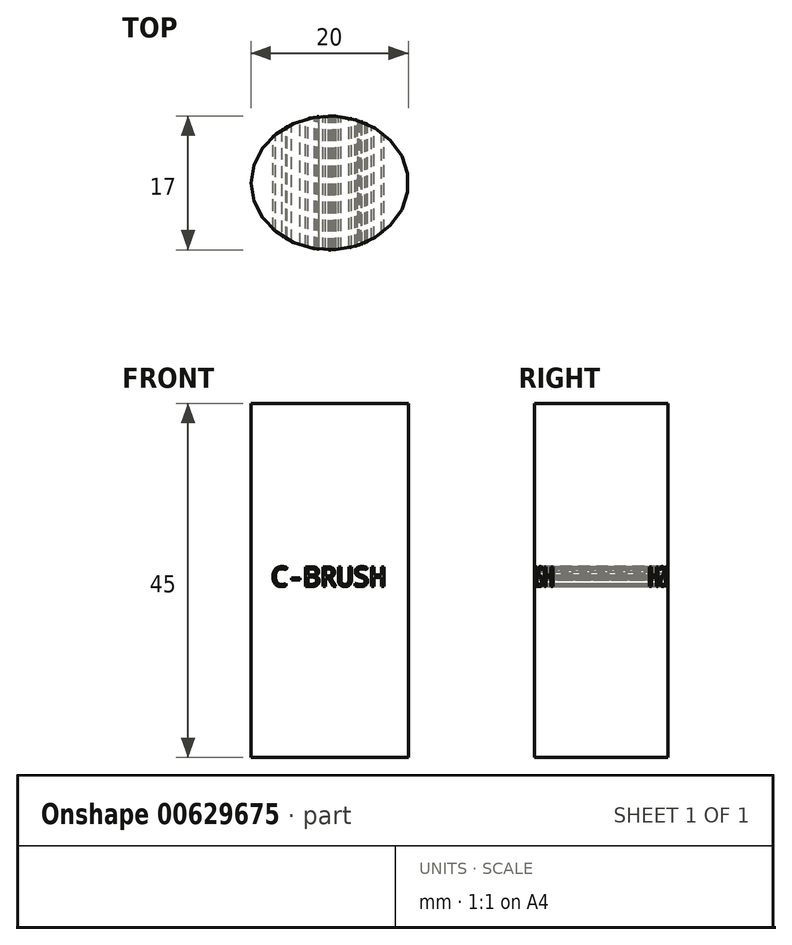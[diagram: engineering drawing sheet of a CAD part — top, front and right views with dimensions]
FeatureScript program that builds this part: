
annotation { "Feature Type Name" : "Feature", "Feature Type Description" : "" }
export const myFeature = defineFeature(function(context is Context, id is Id, definition is map)
    precondition{}
    {
        {
            var Q0;
            Q0=qCreatedBy(makeId("Top.planeOp"),FACE);
            var sketch = newSketch(context, id + "F0", { "sketchPlane" : qUnion([Q0])});
            skEllipse(sketch, "E0", {"center": v(0, 0) * mm, "majorRadius": 10 * mm, "minorRadius": 8.5 * mm, "majorAxis": v(-1, 0)});
            skFitSpline(sketch, "E1.0", {"points": [v(-11.96, 1.07) * mm, v(-12.02, 0) * mm, v(-11.96, -1.07) * mm, v(-11.71, -2.47) * mm, v(-11.23, -3.82) * mm, v(-10.53, -5.08) * mm, v(-9.7, -6.27) * mm, v(-8.42, -7.58) * mm, v(-6.9, -8.65) * mm, v(-5.55, -9.33) * mm, v(-4.14, -9.9) * mm, v(-2.67, -10.28) * mm, v(-1.15, -10.47) * mm, v(0, -10.52) * mm, v(1.15, -10.47) * mm, v(2.67, -10.28) * mm, v(4.14, -9.9) * mm, v(5.55, -9.33) * mm, v(6.9, -8.65) * mm, v(8.42, -7.58) * mm, v(9.7, -6.27) * mm, v(10.53, -5.08) * mm, v(11.23, -3.82) * mm, v(11.71, -2.47) * mm, v(11.96, -1.07) * mm, v(12.02, 0) * mm, v(11.96, 1.07) * mm, v(11.71, 2.47) * mm, v(11.23, 3.82) * mm, v(10.53, 5.08) * mm, v(9.7, 6.27) * mm, v(8.42, 7.58) * mm, v(6.9, 8.65) * mm, v(5.55, 9.33) * mm, v(4.14, 9.9) * mm, v(2.67, 10.28) * mm, v(1.15, 10.47) * mm, v(0, 10.52) * mm, v(-1.15, 10.47) * mm, v(-2.67, 10.28) * mm, v(-4.14, 9.9) * mm, v(-5.55, 9.33) * mm, v(-6.9, 8.65) * mm, v(-8.42, 7.58) * mm, v(-9.7, 6.27) * mm, v(-10.53, 5.08) * mm, v(-11.23, 3.82) * mm, v(-11.71, 2.47) * mm, v(-11.96, 1.07) * mm, v(-12.02, 0) * mm, v(-11.96, -1.07) * mm, v(-11.96, 1.07) * mm]});
            skSolve(sketch);
        }
        {
            var Q0;
            Q0=qSketchRegion(id+"F0",true);
            extrude(context, id + "F1", {"entities" : qUnion([Q0]), "depth" : 45 * mm, "offsetDistance" : 25 * mm});
        }
        {
            var Q0;
            Q0=qCreatedBy(makeId("Front.planeOp"),FACE);
            var sketch = newSketch(context, id + "F2", { "sketchPlane" : qUnion([Q0])});
            skText(sketch, "E2", { "text": "C-BRUSH", "fontName": "DroidSansMono.ttf"});
            const initialGuessF2  = {"E2": [-0.00744, 0.02175, 1, 0, 0.0025]};
            skSetInitialGuess(sketch, initialGuessF2);
            skSolve(sketch);
        }
        {
            var Q0;
            Q0=qSketchRegion(id+"F2",true);
            extrude(context, id + "F3", {"entities" : qUnion([Q0]), "operationType" : NewBodyOperationType.REMOVE, "endBound" : BoundingType.SYMMETRIC, "depth" : 25 * mm, "offsetDistance" : 25 * mm});
        }
    });
